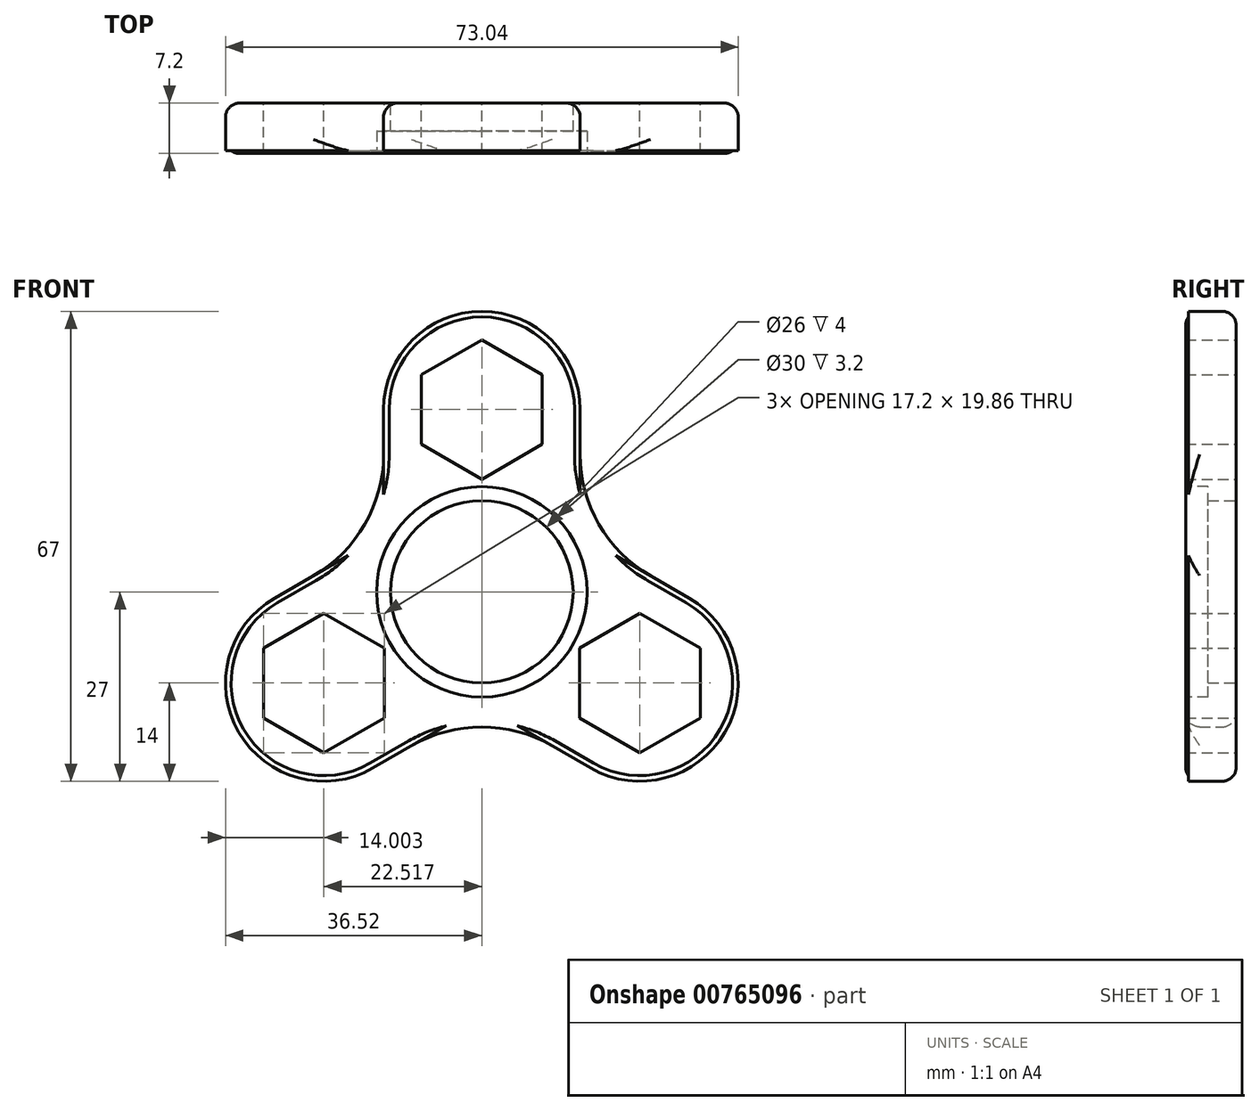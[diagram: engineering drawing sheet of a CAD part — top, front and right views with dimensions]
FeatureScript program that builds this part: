
annotation { "Feature Type Name" : "Feature", "Feature Type Description" : "" }
export const myFeature = defineFeature(function(context is Context, id is Id, definition is map)
    precondition{}
    {
        {
            var Q0;
            Q0=qCreatedBy(makeId("Front.planeOp"),FACE);
            var sketch = newSketch(context, id + "F0", { "sketchPlane" : qUnion([Q0])});
            skCircle(sketch, "E0", {"center": v(0, 0) * mm, "radius": 13 * mm});
            skCircle(sketch, "E1.cCircle", {"center": v(0, 26) * mm, "radius": 8.6 * mm, "construction": true});
            skLineSegment(sketch, "E1.0", {"start": v(8.6, 30.97) * mm, "end": v(8.6, 21.03) * mm});
            skLineSegment(sketch, "E1.1", {"start": v(8.6, 21.03) * mm, "end": v(0, 16.07) * mm});
            skLineSegment(sketch, "E1.2", {"start": v(0, 16.07) * mm, "end": v(-8.6, 21.03) * mm});
            skLineSegment(sketch, "E1.3", {"start": v(-8.6, 21.03) * mm, "end": v(-8.6, 30.97) * mm});
            skLineSegment(sketch, "E1.4", {"start": v(-8.6, 30.97) * mm, "end": v(0, 35.93) * mm});
            skLineSegment(sketch, "E1.5", {"start": v(0, 35.93) * mm, "end": v(8.6, 30.97) * mm});
            skPoint(sketch, "E1.0.midPoint", {"position": v(8.6, 26) * mm});
            skArc(sketch, "E2", {"start": v(14, 26) * mm, "mid": v(0, 40) * mm, "end": v(-14, 26) * mm});
            skLineSegment(sketch, "E3", {"start": v(0, 0) * mm, "end": v(0, 12) * mm, "construction": true});
            skLineSegment(sketch, "E4", {"start": v(-14, 26) * mm, "end": v(-14, 8.08) * mm});
            skLineSegment(sketch, "E5.MirrorCS", {"start": v(14, 26) * mm, "end": v(14, 8.08) * mm});
            skPoint(sketch, "E6.orphan", {"position": v(7, 6.12) * mm});
            skPoint(sketch, "E7.orphan", {"position": v(14, 0) * mm});
            skArc(sketch, "E8.1.0", {"start": v(-29.52, -0.88) * mm, "mid": v(-34.64, -20) * mm, "end": v(-15.52, -25.12) * mm});
            skLineSegment(sketch, "E8.1.1", {"start": v(-15.52, -25.12) * mm, "end": v(0, -16.17) * mm});
            skLineSegment(sketch, "E8.1.2", {"start": v(-29.52, -0.88) * mm, "end": v(-14, 8.08) * mm});
            skLineSegment(sketch, "E8.1.3", {"start": v(-31.12, -17.97) * mm, "end": v(-31.12, -8.03) * mm});
            skLineSegment(sketch, "E8.1.4", {"start": v(-22.52, -22.93) * mm, "end": v(-31.12, -17.97) * mm});
            skLineSegment(sketch, "E8.1.5", {"start": v(-13.92, -17.97) * mm, "end": v(-22.52, -22.93) * mm});
            skLineSegment(sketch, "E8.1.6", {"start": v(-13.92, -8.03) * mm, "end": v(-13.92, -17.97) * mm});
            skLineSegment(sketch, "E8.1.7", {"start": v(-22.52, -3.07) * mm, "end": v(-13.92, -8.03) * mm});
            skLineSegment(sketch, "E8.1.8", {"start": v(-31.12, -8.03) * mm, "end": v(-22.52, -3.07) * mm});
            skArc(sketch, "E8.2.0", {"start": v(15.52, -25.12) * mm, "mid": v(34.64, -20) * mm, "end": v(29.52, -0.88) * mm});
            skLineSegment(sketch, "E8.2.1", {"start": v(29.52, -0.88) * mm, "end": v(14, 8.08) * mm});
            skLineSegment(sketch, "E8.2.2", {"start": v(15.52, -25.12) * mm, "end": v(0, -16.17) * mm});
            skLineSegment(sketch, "E8.2.3", {"start": v(31.12, -17.97) * mm, "end": v(22.52, -22.93) * mm});
            skLineSegment(sketch, "E8.2.4", {"start": v(31.12, -8.03) * mm, "end": v(31.12, -17.97) * mm});
            skLineSegment(sketch, "E8.2.5", {"start": v(22.52, -3.07) * mm, "end": v(31.12, -8.03) * mm});
            skLineSegment(sketch, "E8.2.6", {"start": v(13.92, -8.03) * mm, "end": v(22.52, -3.07) * mm});
            skLineSegment(sketch, "E8.2.7", {"start": v(13.92, -17.97) * mm, "end": v(13.92, -8.03) * mm});
            skLineSegment(sketch, "E8.2.8", {"start": v(22.52, -22.93) * mm, "end": v(13.92, -17.97) * mm});
            skPoint(sketch, "E9.orphan", {"position": v(-8.8, 11.08) * mm});
            skPoint(sketch, "E10.orphan", {"position": v(14, 2.08) * mm});
            skPoint(sketch, "E11.orphan", {"position": v(-5.2, -13.17) * mm});
            skSolve(sketch);
        }
        {
            var Q0;
            Q0 = qSketchRegion(id + "F0", true);
            extrude(context, id + "F1", {"entities" : qUnion([Q0]), "endBound" : BoundingType.SYMMETRIC, "depth" : 7.2 * mm, "offsetDistance" : 25 * mm});
        }
        {
            var Q0;
            Q0=makeQuery(id+"F1.opExtrude","SWEPT_EDGE",EDGE,{"disambiguationData":[OSD([sQuery(id+"F0.wireOp",EDGE,"E4"),sQuery(id+"F0.wireOp",EDGE,"ace69c63-6c91-483b-ba25-7ab2656af985.1.1")])]});
            var Q1;
            Q1=makeQuery(id+"F1.opExtrude","SWEPT_EDGE",EDGE,{"disambiguationData":[OSD([sQuery(id+"F0.wireOp",EDGE,"E5.MirrorCS"),sQuery(id+"F0.wireOp",EDGE,"ace69c63-6c91-483b-ba25-7ab2656af985.2.0")])]});
            var Q2;
            Q2=makeQuery(id+"F1.opExtrude","SWEPT_EDGE",EDGE,{"disambiguationData":[OSD([sQuery(id+"F0.wireOp",EDGE,"ace69c63-6c91-483b-ba25-7ab2656af985.1.0"),sQuery(id+"F0.wireOp",EDGE,"ace69c63-6c91-483b-ba25-7ab2656af985.2.1")])]});
            var Q3;
            Q3=makeQuery(id+"F1.opExtrude","SWEPT_EDGE",EDGE,{"disambiguationData":[OSD([sQuery(id+"F0.wireOp",EDGE,"E8.1.1"),sQuery(id+"F0.wireOp",EDGE,"E8.2.2")])]});
            fillet(context, id + "F2", {"entities" : qUnion([Q0, Q1, Q2, Q3]), "radius" : 20 * mm, "tangentPropagation" : true, "allowEdgeOverflow" : false});
        }
        {
            var Q0;
            Q0=makeQuery(id+"F1.opExtrude","CAP_EDGE",EDGE,{"disambiguationData":[OSD([sQuery(id+"F0.wireOp",EDGE,"E4")])],"isStart":false});
            fillet(context, id + "F3", {"entities" : qUnion([Q0]), "radius" : 2 * mm, "tangentPropagation" : true, "allowEdgeOverflow" : false});
        }
        {
            var Q0;
            Q0=makeQuery(id+"F1.opExtrude","CAP_EDGE",EDGE,{"disambiguationData":[OSD([sQuery(id+"F0.wireOp",EDGE,"E2")])],"isStart":true});
            fillet(context, id + "F4", {"entities" : qUnion([Q0]), "radius" : 2 * mm, "tangentPropagation" : true, "allowEdgeOverflow" : false});
        }
        {
            var Q0;
            Q0 = qSketchRegion(id + "F0", true);
            extrude(context, id + "F5", {"entities" : qUnion([Q0]), "operationType" : NewBodyOperationType.ADD, "depth" : 3.2 * mm, "offsetDistance" : 25 * mm});
        }
        {
            var Q0;
            Q0=makeQuery(id+"F1.opExtrude","CAP_FACE",FACE,{"disambiguationData":[OSD([sQuery(id+"F0.wireOp",EDGE,"E0"),sQuery(id+"F0.wireOp",EDGE,"E1.0"),sQuery(id+"F0.wireOp",EDGE,"E1.1"),sQuery(id+"F0.wireOp",EDGE,"E1.2"),sQuery(id+"F0.wireOp",EDGE,"E1.3"),sQuery(id+"F0.wireOp",EDGE,"E1.4"),sQuery(id+"F0.wireOp",EDGE,"E1.5"),sQuery(id+"F0.wireOp",EDGE,"E2"),sQuery(id+"F0.wireOp",EDGE,"E4"),sQuery(id+"F0.wireOp",EDGE,"E5.MirrorCS"),sQuery(id+"F0.wireOp",EDGE,"E8.1.0"),sQuery(id+"F0.wireOp",EDGE,"E8.1.1"),sQuery(id+"F0.wireOp",EDGE,"E8.1.2"),sQuery(id+"F0.wireOp",EDGE,"E8.1.3"),sQuery(id+"F0.wireOp",EDGE,"E8.1.4"),sQuery(id+"F0.wireOp",EDGE,"E8.1.5"),sQuery(id+"F0.wireOp",EDGE,"E8.1.6"),sQuery(id+"F0.wireOp",EDGE,"E8.1.7"),sQuery(id+"F0.wireOp",EDGE,"E8.1.8"),sQuery(id+"F0.wireOp",EDGE,"E8.2.0"),sQuery(id+"F0.wireOp",EDGE,"E8.2.1"),sQuery(id+"F0.wireOp",EDGE,"E8.2.2"),sQuery(id+"F0.wireOp",EDGE,"E8.2.3"),sQuery(id+"F0.wireOp",EDGE,"E8.2.4"),sQuery(id+"F0.wireOp",EDGE,"E8.2.5"),sQuery(id+"F0.wireOp",EDGE,"E8.2.6"),sQuery(id+"F0.wireOp",EDGE,"E8.2.7"),sQuery(id+"F0.wireOp",EDGE,"E8.2.8")])],"isStart":false});
            var sketch = newSketch(context, id + "F6", { "sketchPlane" : qUnion([Q0])});
            skCircle(sketch, "E12", {"center": v(0, 0) * mm, "radius": 15 * mm});
            skSolve(sketch);
        }
        {
            var Q0;
            Q0 = qSketchRegion(id + "F6", true);
            extrude(context, id + "F7", {"entities" : qUnion([Q0]), "operationType" : NewBodyOperationType.REMOVE, "oppositeDirection" : true, "depth" : 3.2 * mm, "offsetDistance" : 25 * mm});
        }
    });
